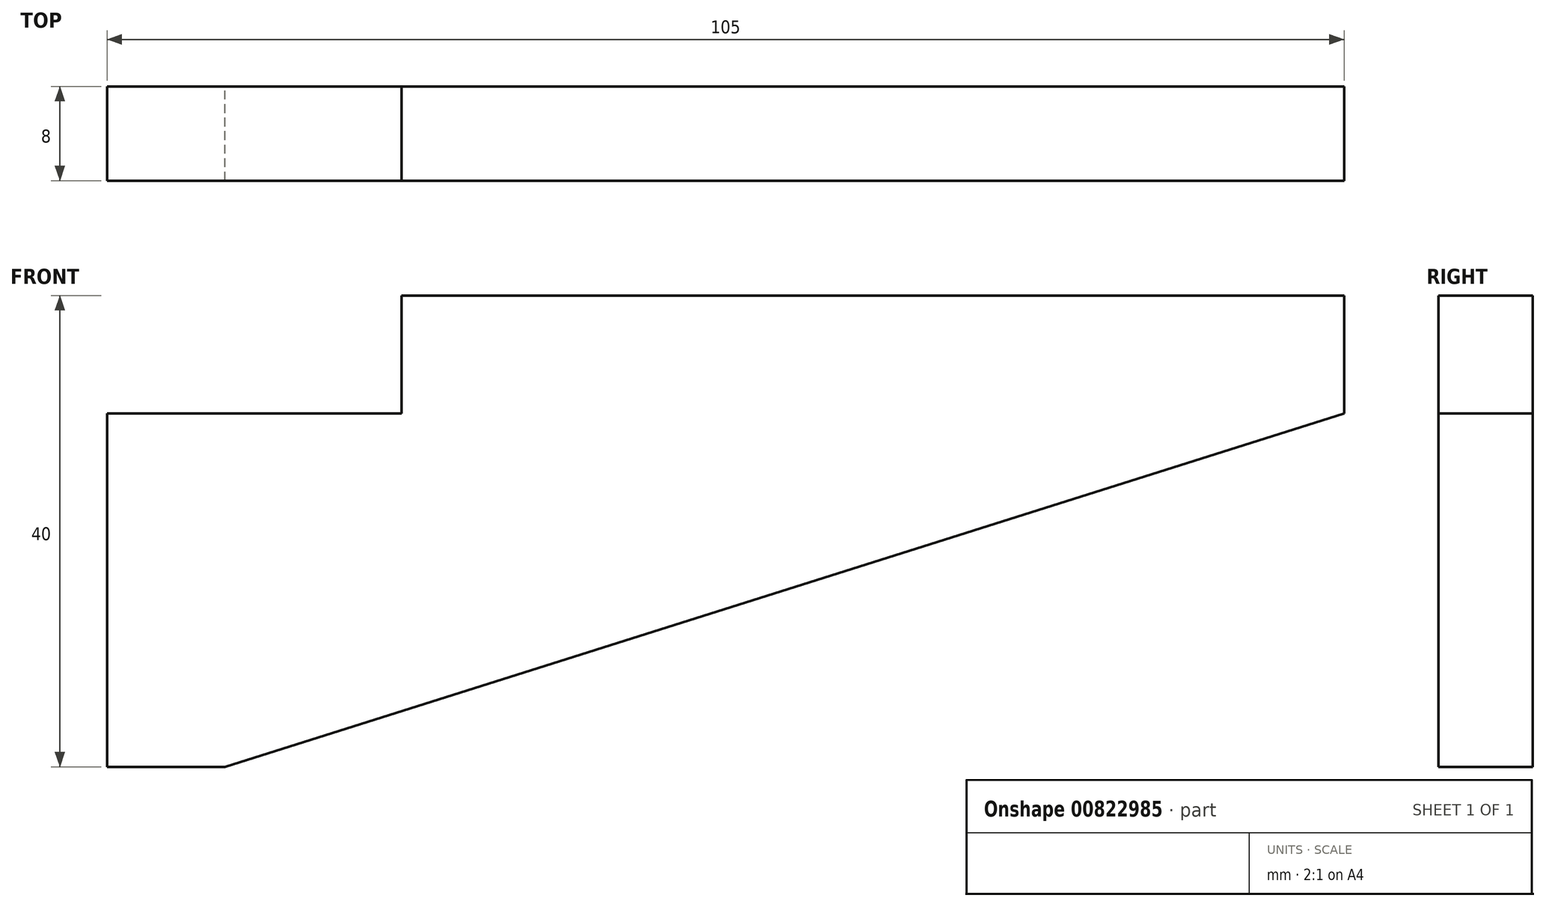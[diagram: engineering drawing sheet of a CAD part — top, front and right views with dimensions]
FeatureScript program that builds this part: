
annotation { "Feature Type Name" : "Feature", "Feature Type Description" : "" }
export const myFeature = defineFeature(function(context is Context, id is Id, definition is map)
    precondition{}
    {
        {
            var Q0;
            Q0=qCreatedBy(makeId("Front.planeOp"),FACE);
            var sketch = newSketch(context, id + "F0", { "sketchPlane" : qUnion([Q0])});
            skLineSegment(sketch, "E0", {"start": v(0, 0) * mm, "end": v(-25, 0) * mm});
            skLineSegment(sketch, "E1", {"start": v(-25, 0) * mm, "end": v(-25, -30) * mm});
            skLineSegment(sketch, "E2", {"start": v(-25, -30) * mm, "end": v(-15, -30) * mm});
            skLineSegment(sketch, "E3", {"start": v(-15, -30) * mm, "end": v(80, 0) * mm});
            skLineSegment(sketch, "E4", {"start": v(80, 0) * mm, "end": v(80, 10) * mm});
            skLineSegment(sketch, "E5", {"start": v(80, 10) * mm, "end": v(0, 10) * mm});
            skLineSegment(sketch, "E6", {"start": v(0, 10) * mm, "end": v(0, 0) * mm});
            skSolve(sketch);
        }
        {
            var Q0;
            Q0 = qSketchRegion(id + "F0", true);
            extrude(context, id + "F1", {"entities" : qUnion([Q0]), "endBound" : BoundingType.SYMMETRIC, "depth" : 8 * mm, "offsetDistance" : 25 * mm});
        }
    });
